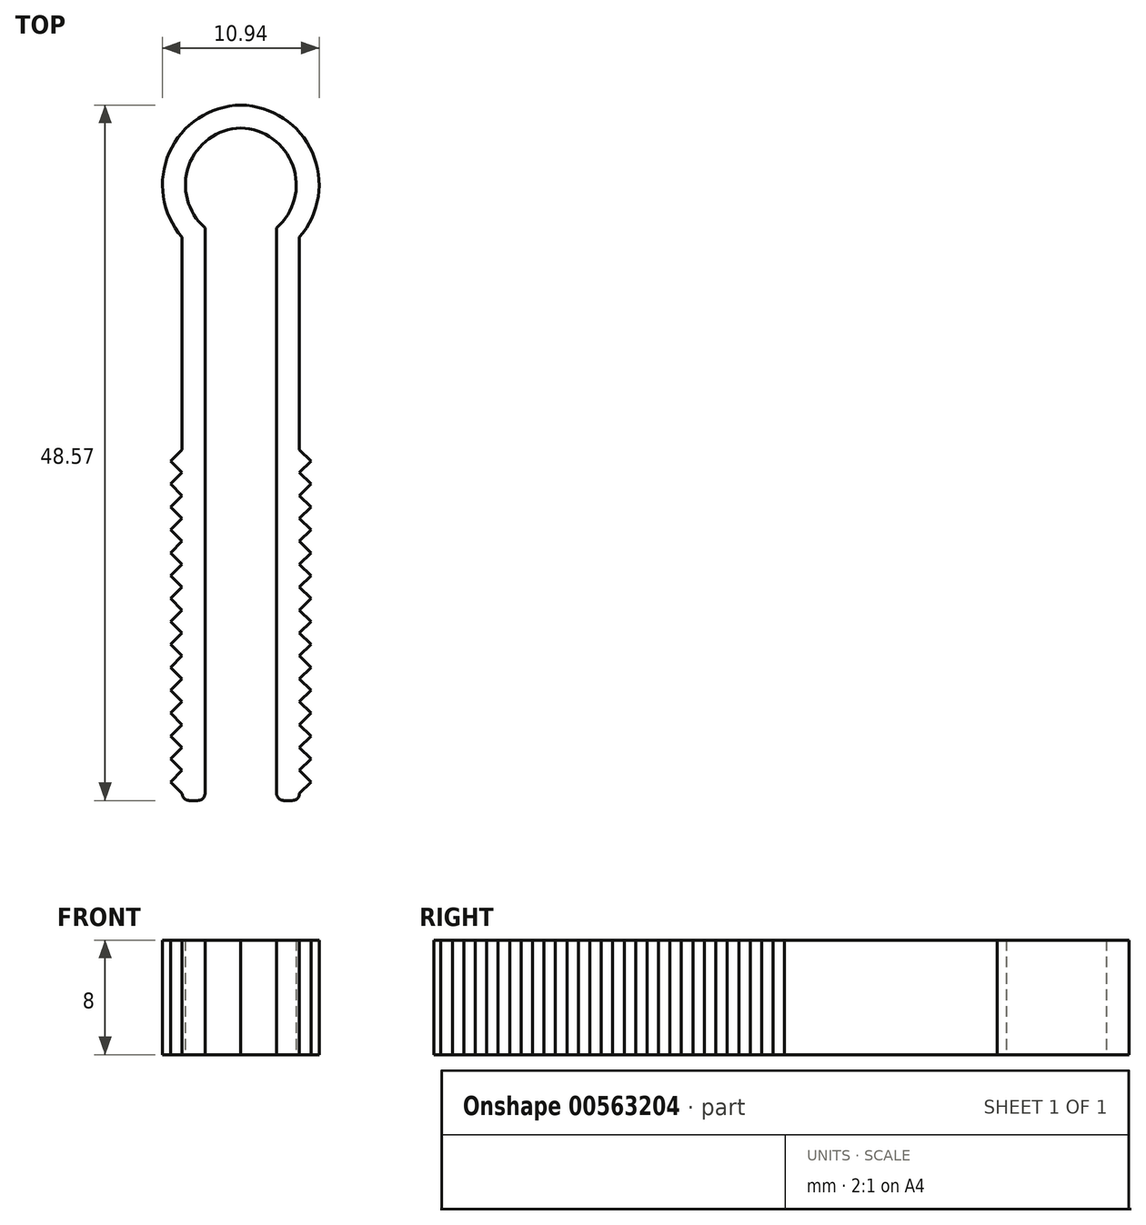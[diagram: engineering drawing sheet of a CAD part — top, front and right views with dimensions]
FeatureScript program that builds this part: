
annotation { "Feature Type Name" : "Feature", "Feature Type Description" : "" }
export const myFeature = defineFeature(function(context is Context, id is Id, definition is map)
    precondition{}
    {
        {
            var Q0;
            Q0=qCreatedBy(makeId("Top.planeOp"),FACE);
            var sketch = newSketch(context, id + "F0", { "sketchPlane" : qUnion([Q0])});
            skArc(sketch, "E0", {"start": v(2.5, 0) * mm, "mid": v(3.64, 4.34) * mm, "end": v(0, 6.97) * mm});
            skLineSegment(sketch, "E1", {"start": v(2.5, 0) * mm, "end": v(2.5, -39.5) * mm});
            skArc(sketch, "E2.0", {"start": v(4.1, -0.66) * mm, "mid": v(4.99, 5.26) * mm, "end": v(0, 8.57) * mm});
            skLineSegment(sketch, "E3.0", {"start": v(4.1, -0.66) * mm, "end": v(4.1, -39.5) * mm});
            skLineSegment(sketch, "E4", {"start": v(3, -40) * mm, "end": v(3.6, -40) * mm});
            skLineSegment(sketch, "E5", {"start": v(0, 0) * mm, "end": v(0, -40) * mm, "construction": true});
            skPoint(sketch, "E6.visualSharp", {"position": v(4.1, -40) * mm});
            skArc(sketch, "E6.filletArc", {"start": v(3.6, -40) * mm, "mid": v(3.95, -39.85) * mm, "end": v(4.1, -39.5) * mm});
            skPoint(sketch, "E7.visualSharp", {"position": v(2.5, -40) * mm});
            skArc(sketch, "E7.filletArc", {"start": v(2.5, -39.5) * mm, "mid": v(2.65, -39.85) * mm, "end": v(3, -40) * mm});
            skLineSegment(sketch, "E8", {"start": v(4.1, -39.5) * mm, "end": v(4.9, -38.7) * mm});
            skLineSegment(sketch, "E9", {"start": v(4.9, -38.7) * mm, "end": v(4.1, -37.9) * mm});
            skPoint(sketch, "E10", {"position": v(0, 0) * mm});
            skLineSegment(sketch, "E11", {"start": v(0, 8.57) * mm, "end": v(0, 6.97) * mm});
            skLineSegment(sketch, "E12", {"start": v(0, 6.97) * mm, "end": v(0, 0) * mm, "construction": true});
            skLineSegment(sketch, "E13.0.1.0", {"start": v(4.1, -37.9) * mm, "end": v(4.9, -37.1) * mm});
            skLineSegment(sketch, "E13.0.1.1", {"start": v(4.9, -37.1) * mm, "end": v(4.1, -36.3) * mm});
            skLineSegment(sketch, "E13.0.2.0", {"start": v(4.1, -36.3) * mm, "end": v(4.9, -35.5) * mm});
            skLineSegment(sketch, "E13.0.2.1", {"start": v(4.9, -35.5) * mm, "end": v(4.1, -34.7) * mm});
            skLineSegment(sketch, "E13.0.3.0", {"start": v(4.1, -34.7) * mm, "end": v(4.9, -33.9) * mm});
            skLineSegment(sketch, "E13.0.3.1", {"start": v(4.9, -33.9) * mm, "end": v(4.1, -33.1) * mm});
            skLineSegment(sketch, "E13.0.4.0", {"start": v(4.1, -33.1) * mm, "end": v(4.9, -32.3) * mm});
            skLineSegment(sketch, "E13.0.4.1", {"start": v(4.9, -32.3) * mm, "end": v(4.1, -31.5) * mm});
            skLineSegment(sketch, "E13.0.5.0", {"start": v(4.1, -31.5) * mm, "end": v(4.9, -30.7) * mm});
            skLineSegment(sketch, "E13.0.5.1", {"start": v(4.9, -30.7) * mm, "end": v(4.1, -29.9) * mm});
            skLineSegment(sketch, "E13.0.6.0", {"start": v(4.1, -29.9) * mm, "end": v(4.9, -29.1) * mm});
            skLineSegment(sketch, "E13.0.6.1", {"start": v(4.9, -29.1) * mm, "end": v(4.1, -28.3) * mm});
            skLineSegment(sketch, "E13.0.7.0", {"start": v(4.1, -28.3) * mm, "end": v(4.9, -27.5) * mm});
            skLineSegment(sketch, "E13.0.7.1", {"start": v(4.9, -27.5) * mm, "end": v(4.1, -26.7) * mm});
            skLineSegment(sketch, "E13.0.8.0", {"start": v(4.1, -26.7) * mm, "end": v(4.9, -25.9) * mm});
            skLineSegment(sketch, "E13.0.8.1", {"start": v(4.9, -25.9) * mm, "end": v(4.1, -25.1) * mm});
            skLineSegment(sketch, "E13.0.9.0", {"start": v(4.1, -25.1) * mm, "end": v(4.9, -24.3) * mm});
            skLineSegment(sketch, "E13.0.9.1", {"start": v(4.9, -24.3) * mm, "end": v(4.1, -23.5) * mm});
            skLineSegment(sketch, "E13.0.10.0", {"start": v(4.1, -23.5) * mm, "end": v(4.9, -22.7) * mm});
            skLineSegment(sketch, "E13.0.10.1", {"start": v(4.9, -22.7) * mm, "end": v(4.1, -21.9) * mm});
            skLineSegment(sketch, "E13.0.11.0", {"start": v(4.1, -21.9) * mm, "end": v(4.9, -21.1) * mm});
            skLineSegment(sketch, "E13.0.11.1", {"start": v(4.9, -21.1) * mm, "end": v(4.1, -20.3) * mm});
            skLineSegment(sketch, "E13.0.12.0", {"start": v(4.1, -20.3) * mm, "end": v(4.9, -19.5) * mm});
            skLineSegment(sketch, "E13.0.12.1", {"start": v(4.9, -19.5) * mm, "end": v(4.1, -18.7) * mm});
            skLineSegment(sketch, "E13.0.13.0", {"start": v(4.1, -18.7) * mm, "end": v(4.9, -17.9) * mm});
            skLineSegment(sketch, "E13.0.13.1", {"start": v(4.9, -17.9) * mm, "end": v(4.1, -17.1) * mm});
            skLineSegment(sketch, "E13.0.14.0", {"start": v(4.1, -17.1) * mm, "end": v(4.9, -16.3) * mm});
            skLineSegment(sketch, "E13.0.14.1", {"start": v(4.9, -16.3) * mm, "end": v(4.1, -15.5) * mm});
            skLineSegment(sketch, "E13.direction2", {"start": v(4.1, -39.5) * mm, "end": v(4.1, -37.9) * mm, "construction": true});
            skLineSegment(sketch, "E14.MirrorCS", {"start": v(-4.1, -39.5) * mm, "end": v(-4.9, -38.7) * mm});
            skArc(sketch, "E15.MirrorCS", {"start": v(-3.6, -40) * mm, "mid": v(-3.95, -39.85) * mm, "end": v(-4.1, -39.5) * mm});
            skLineSegment(sketch, "E16.MirrorCS", {"start": v(-4.1, -37.9) * mm, "end": v(-4.9, -37.1) * mm});
            skLineSegment(sketch, "E17.MirrorCS", {"start": v(-3, -40) * mm, "end": v(-3.6, -40) * mm});
            skLineSegment(sketch, "E18.MirrorCS", {"start": v(-4.1, -39.5) * mm, "end": v(-4.1, -37.9) * mm, "construction": true});
            skLineSegment(sketch, "E19.MirrorCS", {"start": v(-4.9, -38.7) * mm, "end": v(-4.1, -37.9) * mm});
            skLineSegment(sketch, "E20.MirrorCS", {"start": v(-4.9, -17.9) * mm, "end": v(-4.1, -17.1) * mm});
            skLineSegment(sketch, "E21.MirrorCS", {"start": v(-4.1, -18.7) * mm, "end": v(-4.9, -17.9) * mm});
            skLineSegment(sketch, "E22.MirrorCS", {"start": v(-4.1, -31.5) * mm, "end": v(-4.9, -30.7) * mm});
            skLineSegment(sketch, "E23.MirrorCS", {"start": v(-4.1, -33.1) * mm, "end": v(-4.9, -32.3) * mm});
            skLineSegment(sketch, "E24.MirrorCS", {"start": v(-4.9, -21.1) * mm, "end": v(-4.1, -20.3) * mm});
            skLineSegment(sketch, "E25.MirrorCS", {"start": v(-4.1, -25.1) * mm, "end": v(-4.9, -24.3) * mm});
            skLineSegment(sketch, "E26.MirrorCS", {"start": v(-4.9, -19.5) * mm, "end": v(-4.1, -18.7) * mm});
            skLineSegment(sketch, "E27.MirrorCS", {"start": v(-4.1, -36.3) * mm, "end": v(-4.9, -35.5) * mm});
            skLineSegment(sketch, "E28.MirrorCS", {"start": v(-4.9, -33.9) * mm, "end": v(-4.1, -33.1) * mm});
            skLineSegment(sketch, "E29.MirrorCS", {"start": v(-4.9, -32.3) * mm, "end": v(-4.1, -31.5) * mm});
            skLineSegment(sketch, "E30.MirrorCS", {"start": v(-4.9, -37.1) * mm, "end": v(-4.1, -36.3) * mm});
            skLineSegment(sketch, "E31.MirrorCS", {"start": v(-4.1, -26.7) * mm, "end": v(-4.9, -25.9) * mm});
            skLineSegment(sketch, "E32.MirrorCS", {"start": v(-4.1, -20.3) * mm, "end": v(-4.9, -19.5) * mm});
            skArc(sketch, "E33.MirrorCS", {"start": v(-2.5, -39.5) * mm, "mid": v(-2.65, -39.85) * mm, "end": v(-3, -40) * mm});
            skLineSegment(sketch, "E34.MirrorCS", {"start": v(-4.9, -25.9) * mm, "end": v(-4.1, -25.1) * mm});
            skLineSegment(sketch, "E35.MirrorCS", {"start": v(-4.1, -17.1) * mm, "end": v(-4.9, -16.3) * mm});
            skLineSegment(sketch, "E36.MirrorCS", {"start": v(-4.9, -27.5) * mm, "end": v(-4.1, -26.7) * mm});
            skLineSegment(sketch, "E37.MirrorCS", {"start": v(-4.9, -24.3) * mm, "end": v(-4.1, -23.5) * mm});
            skLineSegment(sketch, "E38.MirrorCS", {"start": v(-4.1, -34.7) * mm, "end": v(-4.9, -33.9) * mm});
            skLineSegment(sketch, "E39.MirrorCS", {"start": v(-4.9, -22.7) * mm, "end": v(-4.1, -21.9) * mm});
            skLineSegment(sketch, "E40.MirrorCS", {"start": v(-4.1, -29.9) * mm, "end": v(-4.9, -29.1) * mm});
            skLineSegment(sketch, "E41.MirrorCS", {"start": v(-4.9, -16.3) * mm, "end": v(-4.1, -15.5) * mm});
            skLineSegment(sketch, "E42.MirrorCS", {"start": v(-4.1, -23.5) * mm, "end": v(-4.9, -22.7) * mm});
            skLineSegment(sketch, "E43.MirrorCS", {"start": v(-4.1, -21.9) * mm, "end": v(-4.9, -21.1) * mm});
            skLineSegment(sketch, "E44.MirrorCS", {"start": v(-4.1, -28.3) * mm, "end": v(-4.9, -27.5) * mm});
            skLineSegment(sketch, "E45.MirrorCS", {"start": v(-4.9, -30.7) * mm, "end": v(-4.1, -29.9) * mm});
            skLineSegment(sketch, "E46.MirrorCS", {"start": v(-4.9, -35.5) * mm, "end": v(-4.1, -34.7) * mm});
            skLineSegment(sketch, "E47.MirrorCS", {"start": v(-4.9, -29.1) * mm, "end": v(-4.1, -28.3) * mm});
            skLineSegment(sketch, "E48.MirrorCS", {"start": v(-2.5, 0) * mm, "end": v(-2.5, -39.5) * mm});
            skArc(sketch, "E49.MirrorCS", {"start": v(-2.5, 0) * mm, "mid": v(-3.64, 4.34) * mm, "end": v(0, 6.97) * mm});
            skPoint(sketch, "E50.MirrorP", {"position": v(-2.5, -40) * mm});
            skPoint(sketch, "E51.MirrorP", {"position": v(-4.1, -40) * mm});
            skArc(sketch, "E52.MirrorCS", {"start": v(-4.1, -0.66) * mm, "mid": v(-4.99, 5.26) * mm, "end": v(0, 8.57) * mm});
            skLineSegment(sketch, "E53.MirrorCS", {"start": v(-4.1, -0.66) * mm, "end": v(-4.1, -39.5) * mm});
            skSolve(sketch);
        }
        {
            var Q0;
            Q0 = qSketchRegion(id + "F0", true);
            extrude(context, id + "F1", {"entities" : qUnion([Q0]), "depth" : 8 * mm, "offsetDistance" : 25 * mm});
        }
    });
